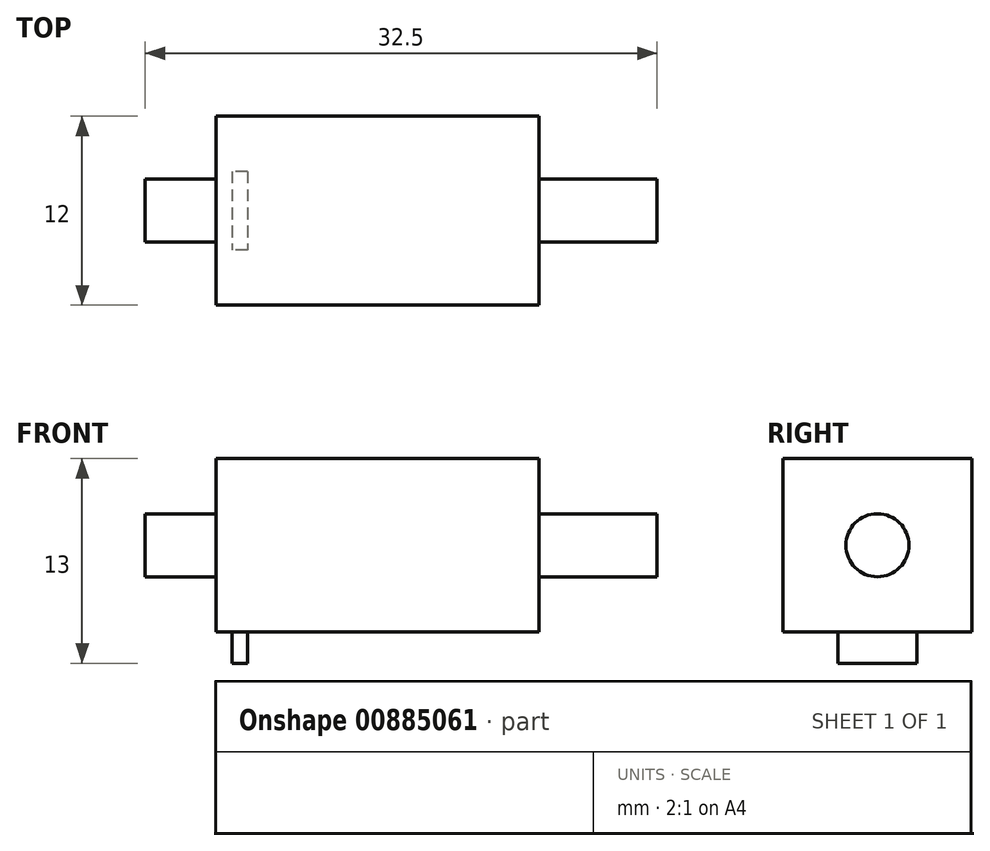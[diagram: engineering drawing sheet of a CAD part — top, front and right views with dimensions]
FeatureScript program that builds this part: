
annotation { "Feature Type Name" : "Feature", "Feature Type Description" : "" }
export const myFeature = defineFeature(function(context is Context, id is Id, definition is map)
    precondition{}
    {
        {
            var Q0;
            Q0=qCreatedBy(makeId("Top.planeOp"),FACE);
            var sketch = newSketch(context, id + "F0", { "sketchPlane" : qUnion([Q0])});
            skLineSegment(sketch, "E0.bottom", {"start": v(10.25, 6) * mm, "end": v(-10.25, 6) * mm});
            skLineSegment(sketch, "E0.top", {"start": v(10.25, -6) * mm, "end": v(-10.25, -6) * mm});
            skLineSegment(sketch, "E0.left", {"start": v(10.25, 6) * mm, "end": v(10.25, -6) * mm});
            skLineSegment(sketch, "E0.right", {"start": v(-10.25, 6) * mm, "end": v(-10.25, -6) * mm});
            skPoint(sketch, "E0.middle", {"position": v(0, 0) * mm});
            skSolve(sketch);
        }
        {
            var Q0;
            Q0 = qSketchRegion(id + "F0", true);
            extrude(context, id + "F1", {"entities" : qUnion([Q0]), "depth" : 5.5 * mm, "offsetDistance" : 25 * mm, "hasSecondDirection" : true, "secondDirectionOppositeDirection" : true, "secondDirectionDepth" : 5.5 * mm});
        }
        {
            var Q0;
            Q0=makeQuery(id+"F1.opExtrude","SWEPT_FACE",FACE,{"disambiguationData":[OSD([sQuery(id+"F0.wireOp",EDGE,"E0.right")])]});
            var sketch = newSketch(context, id + "F2", { "sketchPlane" : qUnion([Q0])});
            skCircle(sketch, "E1", {"center": v(0, 0) * mm, "radius": 2 * mm});
            skSolve(sketch);
        }
        {
            var Q0;
            Q0 = qSketchRegion(id + "F2", true);
            extrude(context, id + "F3", {"entities" : qUnion([Q0]), "operationType" : NewBodyOperationType.ADD, "depth" : 4.5 * mm, "offsetDistance" : 25 * mm});
        }
        {
            var Q0;
            Q0=makeQuery(id+"F1.opExtrude","SWEPT_FACE",FACE,{"disambiguationData":[OSD([sQuery(id+"F0.wireOp",EDGE,"E0.left")])]});
            var sketch = newSketch(context, id + "F4", { "sketchPlane" : qUnion([Q0])});
            skCircle(sketch, "E2", {"center": v(0, 0) * mm, "radius": 2 * mm});
            skSolve(sketch);
        }
        {
            var Q0;
            Q0=makeQuery(id+"F4.imprint","IMPRINT",FACE,{"disambiguationData":[TD([[makeQuery(id+"F4.imprint","IMPRINT",EDGE,{"derivedFrom":sQuery(id+"F4.wireOp",EDGE,"E2")}),1.0]])]});
            extrude(context, id + "F5", {"entities" : qUnion([Q0]), "operationType" : NewBodyOperationType.ADD, "depth" : 7.5 * mm, "offsetDistance" : 25 * mm});
        }
        {
            var Q0;
            Q0=makeQuery(id+"F1.opExtrude","CAP_FACE",FACE,{"disambiguationData":[OSD([sQuery(id+"F0.wireOp",EDGE,"E0.bottom"),sQuery(id+"F0.wireOp",EDGE,"E0.top"),sQuery(id+"F0.wireOp",EDGE,"E0.left"),sQuery(id+"F0.wireOp",EDGE,"E0.right")])],"isStart":true});
            var sketch = newSketch(context, id + "F6", { "sketchPlane" : qUnion([Q0])});
            skLineSegment(sketch, "E3.bottom", {"start": v(-8.25, -2.5) * mm, "end": v(-9.25, -2.5) * mm});
            skLineSegment(sketch, "E3.top", {"start": v(-8.25, 2.5) * mm, "end": v(-9.25, 2.5) * mm});
            skLineSegment(sketch, "E3.left", {"start": v(-8.25, -2.5) * mm, "end": v(-8.25, 2.5) * mm});
            skLineSegment(sketch, "E3.right", {"start": v(-9.25, -2.5) * mm, "end": v(-9.25, 2.5) * mm});
            skPoint(sketch, "E3.middle", {"position": v(-8.75, 0) * mm});
            skPoint(sketch, "E3.middle.positionSnap0", {"position": v(-10.25, 0) * mm});
            skPoint(sketch, "E3.centerSnap0", {"position": v(-10.25, 0) * mm});
            skSolve(sketch);
        }
        {
            var Q0;
            Q0 = qSketchRegion(id + "F6", true);
            extrude(context, id + "F7", {"entities" : qUnion([Q0]), "operationType" : NewBodyOperationType.ADD, "depth" : 2 * mm, "offsetDistance" : 25 * mm});
        }
    });
